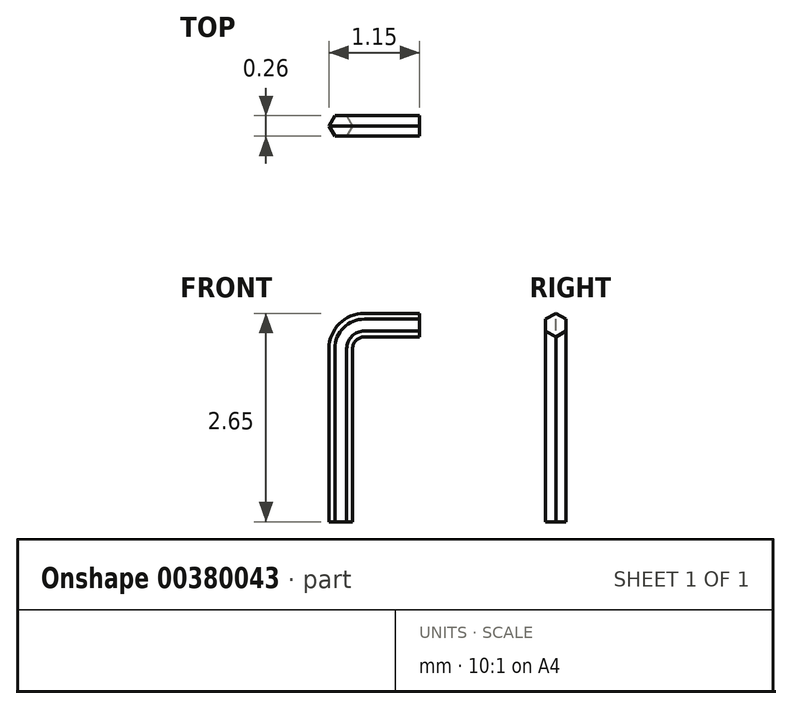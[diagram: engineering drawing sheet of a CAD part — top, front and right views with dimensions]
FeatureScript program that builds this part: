
annotation { "Feature Type Name" : "Feature", "Feature Type Description" : "" }
export const myFeature = defineFeature(function(context is Context, id is Id, definition is map)
    precondition{}
    {
        {
            var Q0;
            Q0=qCreatedBy(makeId("Front.planeOp"),FACE);
            var sketch = newSketch(context, id + "F0", { "sketchPlane" : qUnion([Q0])});
            skLineSegment(sketch, "E0", {"start": v(0, 0) * mm, "end": v(0, 2.2) * mm});
            skLineSegment(sketch, "E1", {"start": v(0.3, 2.5) * mm, "end": v(1, 2.5) * mm});
            skPoint(sketch, "E2.visualSharp", {"position": v(0, 2.5) * mm});
            skArc(sketch, "E2.filletArc", {"start": v(0.3, 2.5) * mm, "mid": v(0.09, 2.41) * mm, "end": v(0, 2.2) * mm});
            skSolve(sketch);
        }
        {
            var Q0;
            Q0=qCreatedBy(makeId("Top.planeOp"),FACE);
            var sketch = newSketch(context, id + "F1", { "sketchPlane" : qUnion([Q0])});
            skCircle(sketch, "E3.cCircle", {"center": v(0, 0) * mm, "radius": 0.13 * mm, "construction": true});
            skLineSegment(sketch, "E3.0", {"start": v(-0.07, 0.13) * mm, "end": v(0.07, 0.13) * mm});
            skLineSegment(sketch, "E3.1", {"start": v(0.07, 0.13) * mm, "end": v(0.15, 0) * mm});
            skLineSegment(sketch, "E3.2", {"start": v(0.15, 0) * mm, "end": v(0.08, -0.13) * mm});
            skLineSegment(sketch, "E3.3", {"start": v(0.08, -0.13) * mm, "end": v(-0.07, -0.13) * mm});
            skLineSegment(sketch, "E3.4", {"start": v(-0.07, -0.13) * mm, "end": v(-0.15, 0) * mm});
            skLineSegment(sketch, "E3.5", {"start": v(-0.15, 0) * mm, "end": v(-0.07, 0.13) * mm});
            skPoint(sketch, "E3.0.midPoint", {"position": v(0, 0.13) * mm});
            skSolve(sketch);
        }
        {
            var Q0;
            Q0=makeQuery(id+"F1.imprint","IMPRINT",FACE,{"disambiguationData":[TD([[makeQuery(id+"F1.imprint","IMPRINT",EDGE,{"derivedFrom":sQuery(id+"F1.wireOp",EDGE,"E3.0")}),-1.0]])]});
            var Q1;
            Q1=sQuery(id+"F0.wireOp",EDGE,"E0");
            var Q2;
            Q2=sQuery(id+"F0.wireOp",EDGE,"E2.filletArc");
            var Q3;
            Q3=sQuery(id+"F0.wireOp",EDGE,"E1");
            sweep(context, id + "F2", {"profiles" : qUnion([Q0]), "path" : qUnion([Q1, Q2, Q3])});
        }
    });
